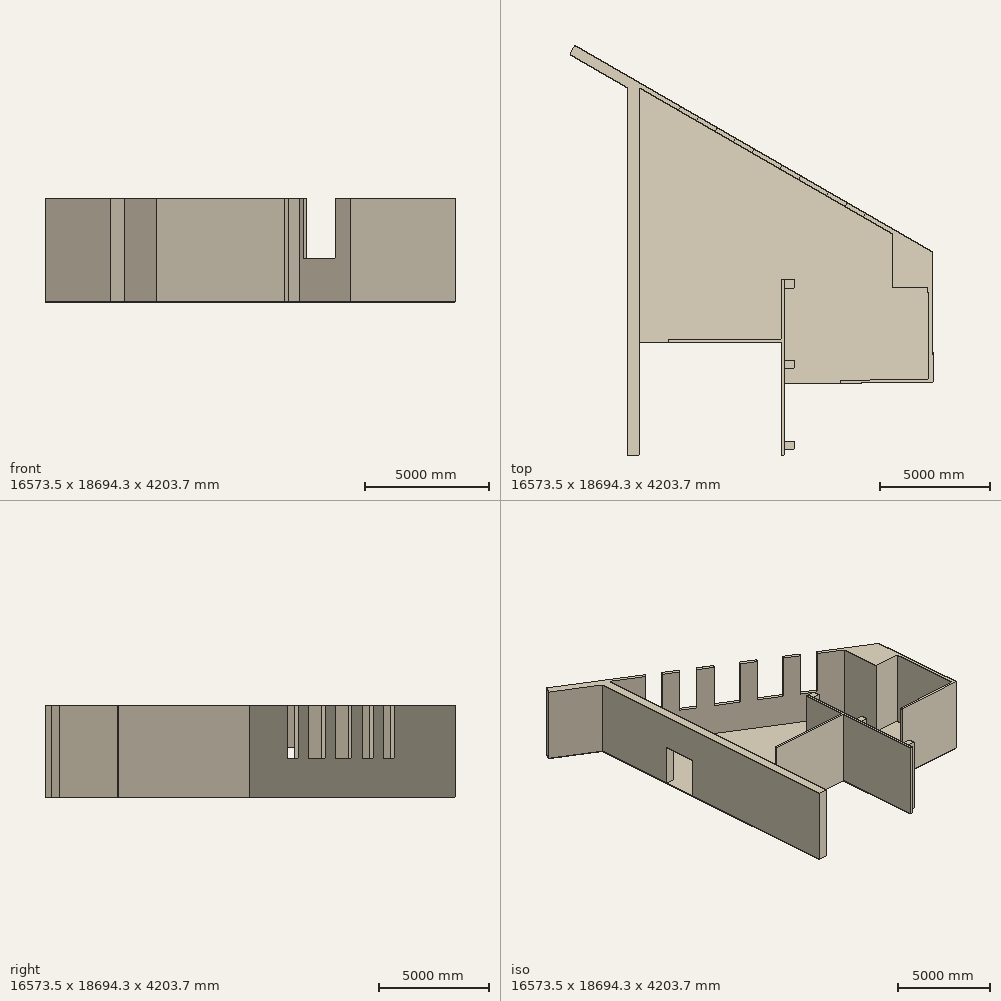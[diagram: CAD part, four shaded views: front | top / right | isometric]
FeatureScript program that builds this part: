
annotation { "Feature Type Name" : "Feature", "Feature Type Description" : "" }
export const myFeature = defineFeature(function(context is Context, id is Id, definition is map)
    precondition{}
    {
        {
            var Q0;
            Q0=qCreatedBy(makeId("Top.planeOp"),FACE);
            var sketch = newSketch(context, id + "F0", { "sketchPlane" : qUnion([Q0])});
            skLineSegment(sketch, "E0.bottom", {"start": v(0, 0) * mm, "end": v(546.1, 0) * mm});
            skLineSegment(sketch, "E0.top", {"start": v(0, 4953) * mm, "end": v(546.1, 4953) * mm});
            skLineSegment(sketch, "E0.left", {"start": v(0, 0) * mm, "end": v(0, 4953) * mm});
            skLineSegment(sketch, "E0.right", {"start": v(546.1, 0) * mm, "end": v(546.1, 4953) * mm});
            skSolve(sketch);
        }
        {
            var Q0;
            Q0 = qSketchRegion(id + "F0", true);
            extrude(context, id + "F1", {"entities" : qUnion([Q0]), "depth" : 4178.3 * mm, "offsetDistance" : 25.4 * mm});
        }
        {
            var Q0;
            Q0=makeQuery(id+"F1.opExtrude","CAP_FACE",FACE,{"disambiguationData":[OSD([sQuery(id+"F0.wireOp",EDGE,"E0.bottom"),sQuery(id+"F0.wireOp",EDGE,"E0.top"),sQuery(id+"F0.wireOp",EDGE,"E0.left"),sQuery(id+"F0.wireOp",EDGE,"E0.right")])],"isStart":false});
            var sketch = newSketch(context, id + "F2", { "sketchPlane" : qUnion([Q0])});
            skLineSegment(sketch, "E1", {"start": v(546.1, 4953) * mm, "end": v(2322.36, 3927.47) * mm});
            skLineSegment(sketch, "E2", {"start": v(2322.36, 3927.47) * mm, "end": v(2423.96, 4103.45) * mm});
            skLineSegment(sketch, "E3", {"start": v(2423.96, 4103.45) * mm, "end": v(-2401.52, 6889.44) * mm});
            skLineSegment(sketch, "E4", {"start": v(-2401.52, 6889.44) * mm, "end": v(-2639.65, 6477) * mm});
            skLineSegment(sketch, "E5", {"start": v(-2639.65, 6477) * mm, "end": v(0, 4953) * mm});
            skSolve(sketch);
        }
        {
            var Q0;
            Q0=makeQuery(id+"F2.imprint","IMPRINT",FACE,{"disambiguationData":[TD([[makeQuery(id+"F2.imprint","IMPRINT",EDGE,{"derivedFrom":sQuery(id+"F2.wireOp",EDGE,"E1")}),1.0]])]});
            var Q1;
            Q1=makeQuery(id+"F1.opExtrude","CAP_FACE",FACE,{"disambiguationData":[OSD([sQuery(id+"F0.wireOp",EDGE,"E0.bottom"),sQuery(id+"F0.wireOp",EDGE,"E0.top"),sQuery(id+"F0.wireOp",EDGE,"E0.left"),sQuery(id+"F0.wireOp",EDGE,"E0.right")])],"isStart":true});
            extrude(context, id + "F3", {"entities" : qUnion([Q0]), "operationType" : NewBodyOperationType.ADD, "endBound" : BoundingType.UP_TO_SURFACE, "oppositeDirection" : true, "depth" : 25.4 * mm, "endBoundEntityFace" : qUnion([Q1]), "offsetDistance" : 25.4 * mm});
        }
        {
            var Q0;
            Q0=makeQuery(id+"F3.opExtrude","SWEPT_FACE",FACE,{"disambiguationData":[OSD([sQuery(id+"F2.wireOp",EDGE,"E2")])]});
            var sketch = newSketch(context, id + "F4", { "sketchPlane" : qUnion([Q0])});
            skLineSegment(sketch, "E6.bottom", {"start": v(4562.47, 0) * mm, "end": v(4765.67, 0) * mm});
            skLineSegment(sketch, "E6.top", {"start": v(4562.47, 1765.3) * mm, "end": v(4765.67, 1765.3) * mm});
            skLineSegment(sketch, "E6.left", {"start": v(4562.47, 0) * mm, "end": v(4562.47, 1765.3) * mm});
            skLineSegment(sketch, "E6.right", {"start": v(4765.67, 0) * mm, "end": v(4765.67, 1765.3) * mm});
            skSolve(sketch);
        }
        {
            var Q0;
            Q0=makeQuery(id+"F4.imprint","IMPRINT",FACE,{"disambiguationData":[TD([[makeQuery(id+"F4.imprint","IMPRINT",EDGE,{"derivedFrom":sQuery(id+"F4.wireOp",EDGE,"E6.bottom")}),-1.0]])]});
            extrude(context, id + "F5", {"entities" : qUnion([Q0]), "operationType" : NewBodyOperationType.ADD, "depth" : 958.85 * mm, "offsetDistance" : 25.4 * mm});
        }
        {
            var Q0;
            Q0=makeQuery(id+"F5.opExtrude","CAP_FACE",FACE,{"disambiguationData":[OSD([sQuery(id+"F4.wireOp",EDGE,"E6.bottom"),sQuery(id+"F4.wireOp",EDGE,"E6.top"),sQuery(id+"F4.wireOp",EDGE,"E6.left"),sQuery(id+"F4.wireOp",EDGE,"E6.right")])],"isStart":false});
            var sketch = newSketch(context, id + "F6", { "sketchPlane" : qUnion([Q0])});
            skLineSegment(sketch, "E7.bottom", {"start": v(4562.47, 0) * mm, "end": v(4765.67, 0) * mm});
            skLineSegment(sketch, "E7.top", {"start": v(4562.47, 4178.3) * mm, "end": v(4765.67, 4178.3) * mm});
            skLineSegment(sketch, "E7.left", {"start": v(4562.47, 0) * mm, "end": v(4562.47, 4178.3) * mm});
            skLineSegment(sketch, "E7.right", {"start": v(4765.67, 0) * mm, "end": v(4765.67, 4178.3) * mm});
            skSolve(sketch);
        }
        {
            var Q0;
            Q0 = qSketchRegion(id + "F6", true);
            extrude(context, id + "F7", {"entities" : qUnion([Q0]), "operationType" : NewBodyOperationType.ADD, "depth" : 965.2 * mm, "offsetDistance" : 25.4 * mm});
        }
        {
            var Q0;
            Q0=makeQuery(id+"F7.opExtrude","CAP_FACE",FACE,{"disambiguationData":[OSD([sQuery(id+"F6.wireOp",EDGE,"E7.bottom"),sQuery(id+"F6.wireOp",EDGE,"E7.top"),sQuery(id+"F6.wireOp",EDGE,"E7.left"),sQuery(id+"F6.wireOp",EDGE,"E7.right")])],"isStart":false});
            var sketch = newSketch(context, id + "F8", { "sketchPlane" : qUnion([Q0])});
            skLineSegment(sketch, "E8.bottom", {"start": v(4562.47, 1765.3) * mm, "end": v(4765.67, 1765.3) * mm});
            skLineSegment(sketch, "E8.top", {"start": v(4562.47, 0) * mm, "end": v(4765.67, 0) * mm});
            skLineSegment(sketch, "E8.left", {"start": v(4562.47, 1765.3) * mm, "end": v(4562.47, 0) * mm});
            skLineSegment(sketch, "E8.right", {"start": v(4765.67, 1765.3) * mm, "end": v(4765.67, 0) * mm});
            skSolve(sketch);
        }
        {
            var Q0;
            Q0=makeQuery(id+"F8.imprint","IMPRINT",FACE,{"disambiguationData":[TD([[makeQuery(id+"F8.imprint","IMPRINT",EDGE,{"derivedFrom":sQuery(id+"F8.wireOp",EDGE,"E8.bottom")}),-1.0]])]});
            extrude(context, id + "F9", {"entities" : qUnion([Q0]), "operationType" : NewBodyOperationType.ADD, "depth" : 965.2 * mm, "offsetDistance" : 25.4 * mm});
        }
        {
            var Q0;
            Q0=makeQuery(id+"F9.opExtrude","CAP_FACE",FACE,{"disambiguationData":[OSD([sQuery(id+"F8.wireOp",EDGE,"E8.bottom"),sQuery(id+"F8.wireOp",EDGE,"E8.top"),sQuery(id+"F8.wireOp",EDGE,"E8.left"),sQuery(id+"F8.wireOp",EDGE,"E8.right")])],"isStart":false});
            var sketch = newSketch(context, id + "F10", { "sketchPlane" : qUnion([Q0])});
            skLineSegment(sketch, "E9.bottom", {"start": v(4562.47, 0) * mm, "end": v(4765.67, 0) * mm});
            skLineSegment(sketch, "E9.top", {"start": v(4562.47, 4178.3) * mm, "end": v(4765.67, 4178.3) * mm});
            skLineSegment(sketch, "E9.left", {"start": v(4562.47, 0) * mm, "end": v(4562.47, 4178.3) * mm});
            skLineSegment(sketch, "E9.right", {"start": v(4765.67, 0) * mm, "end": v(4765.67, 4178.3) * mm});
            skSolve(sketch);
        }
        {
            var Q0;
            Q0 = qSketchRegion(id + "F10", true);
            extrude(context, id + "F11", {"entities" : qUnion([Q0]), "operationType" : NewBodyOperationType.ADD, "depth" : 977.9 * mm, "offsetDistance" : 25.4 * mm});
        }
        {
            var Q0;
            Q0=makeQuery(id+"F11.opExtrude","CAP_FACE",FACE,{"disambiguationData":[OSD([sQuery(id+"F10.wireOp",EDGE,"E9.bottom"),sQuery(id+"F10.wireOp",EDGE,"E9.top"),sQuery(id+"F10.wireOp",EDGE,"E9.left"),sQuery(id+"F10.wireOp",EDGE,"E9.right")])],"isStart":false});
            var sketch = newSketch(context, id + "F12", { "sketchPlane" : qUnion([Q0])});
            skLineSegment(sketch, "E10.bottom", {"start": v(4562.47, 0) * mm, "end": v(4765.67, 0) * mm});
            skLineSegment(sketch, "E10.top", {"start": v(4562.47, 1765.3) * mm, "end": v(4765.67, 1765.3) * mm});
            skLineSegment(sketch, "E10.left", {"start": v(4562.47, 0) * mm, "end": v(4562.47, 1765.3) * mm});
            skLineSegment(sketch, "E10.right", {"start": v(4765.67, 0) * mm, "end": v(4765.67, 1765.3) * mm});
            skSolve(sketch);
        }
        {
            var Q0;
            Q0 = qSketchRegion(id + "F12", true);
            extrude(context, id + "F13", {"entities" : qUnion([Q0]), "operationType" : NewBodyOperationType.ADD, "depth" : 1473.2 * mm, "offsetDistance" : 25.4 * mm});
        }
        {
            var Q0;
            Q0=makeQuery(id+"F13.opExtrude","CAP_FACE",FACE,{"disambiguationData":[OSD([sQuery(id+"F12.wireOp",EDGE,"E10.bottom"),sQuery(id+"F12.wireOp",EDGE,"E10.top"),sQuery(id+"F12.wireOp",EDGE,"E10.left"),sQuery(id+"F12.wireOp",EDGE,"E10.right")])],"isStart":false});
            var sketch = newSketch(context, id + "F14", { "sketchPlane" : qUnion([Q0])});
            skLineSegment(sketch, "E11.bottom", {"start": v(4562.47, 0) * mm, "end": v(4765.67, 0) * mm});
            skLineSegment(sketch, "E11.top", {"start": v(4562.47, 4178.3) * mm, "end": v(4765.67, 4178.3) * mm});
            skLineSegment(sketch, "E11.left", {"start": v(4562.47, 0) * mm, "end": v(4562.47, 4178.3) * mm});
            skLineSegment(sketch, "E11.right", {"start": v(4765.67, 0) * mm, "end": v(4765.67, 4178.3) * mm});
            skSolve(sketch);
        }
        {
            var Q0;
            Q0 = qSketchRegion(id + "F14", true);
            extrude(context, id + "F15", {"entities" : qUnion([Q0]), "operationType" : NewBodyOperationType.ADD, "depth" : 977.9 * mm, "offsetDistance" : 25.4 * mm});
        }
        {
            var Q0;
            Q0=makeQuery(id+"F15.opExtrude","CAP_FACE",FACE,{"disambiguationData":[OSD([sQuery(id+"F14.wireOp",EDGE,"E11.bottom"),sQuery(id+"F14.wireOp",EDGE,"E11.top"),sQuery(id+"F14.wireOp",EDGE,"E11.left"),sQuery(id+"F14.wireOp",EDGE,"E11.right")])],"isStart":false});
            var sketch = newSketch(context, id + "F16", { "sketchPlane" : qUnion([Q0])});
            skLineSegment(sketch, "E12.bottom", {"start": v(4562.47, 0) * mm, "end": v(4765.67, 0) * mm});
            skLineSegment(sketch, "E12.top", {"start": v(4562.47, 1765.3) * mm, "end": v(4765.67, 1765.3) * mm});
            skLineSegment(sketch, "E12.left", {"start": v(4562.47, 0) * mm, "end": v(4562.47, 1765.3) * mm});
            skLineSegment(sketch, "E12.right", {"start": v(4765.67, 0) * mm, "end": v(4765.67, 1765.3) * mm});
            skSolve(sketch);
        }
        {
            var Q0;
            Q0 = qSketchRegion(id + "F16", true);
            extrude(context, id + "F17", {"entities" : qUnion([Q0]), "operationType" : NewBodyOperationType.ADD, "depth" : 1473.2 * mm, "offsetDistance" : 25.4 * mm});
        }
        {
            var Q0;
            Q0=makeQuery(id+"F17.opExtrude","CAP_FACE",FACE,{"disambiguationData":[OSD([sQuery(id+"F16.wireOp",EDGE,"E12.bottom"),sQuery(id+"F16.wireOp",EDGE,"E12.top"),sQuery(id+"F16.wireOp",EDGE,"E12.left"),sQuery(id+"F16.wireOp",EDGE,"E12.right")])],"isStart":false});
            var sketch = newSketch(context, id + "F18", { "sketchPlane" : qUnion([Q0])});
            skLineSegment(sketch, "E13.bottom", {"start": v(4562.47, 0) * mm, "end": v(4765.67, 0) * mm});
            skLineSegment(sketch, "E13.top", {"start": v(4562.47, 4178.3) * mm, "end": v(4765.67, 4178.3) * mm});
            skLineSegment(sketch, "E13.left", {"start": v(4562.47, 0) * mm, "end": v(4562.47, 4178.3) * mm});
            skLineSegment(sketch, "E13.right", {"start": v(4765.67, 0) * mm, "end": v(4765.67, 4178.3) * mm});
            skSolve(sketch);
        }
        {
            var Q0;
            Q0 = qSketchRegion(id + "F18", true);
            extrude(context, id + "F19", {"entities" : qUnion([Q0]), "operationType" : NewBodyOperationType.ADD, "depth" : 977.9 * mm, "offsetDistance" : 25.4 * mm});
        }
        {
            var Q0;
            Q0=makeQuery(id+"F19.opExtrude","CAP_FACE",FACE,{"disambiguationData":[OSD([sQuery(id+"F18.wireOp",EDGE,"E13.bottom"),sQuery(id+"F18.wireOp",EDGE,"E13.top"),sQuery(id+"F18.wireOp",EDGE,"E13.left"),sQuery(id+"F18.wireOp",EDGE,"E13.right")])],"isStart":false});
            var sketch = newSketch(context, id + "F20", { "sketchPlane" : qUnion([Q0])});
            skLineSegment(sketch, "E14.bottom", {"start": v(4562.47, 0) * mm, "end": v(4765.67, 0) * mm});
            skLineSegment(sketch, "E14.top", {"start": v(4562.47, 1765.3) * mm, "end": v(4765.67, 1765.3) * mm});
            skLineSegment(sketch, "E14.left", {"start": v(4562.47, 0) * mm, "end": v(4562.47, 1765.3) * mm});
            skLineSegment(sketch, "E14.right", {"start": v(4765.67, 0) * mm, "end": v(4765.67, 1765.3) * mm});
            skSolve(sketch);
        }
        {
            var Q0;
            Q0 = qSketchRegion(id + "F20", true);
            extrude(context, id + "F21", {"entities" : qUnion([Q0]), "operationType" : NewBodyOperationType.ADD, "depth" : 958.85 * mm, "offsetDistance" : 25.4 * mm});
        }
        {
            var Q0;
            Q0=makeQuery(id+"F21.opExtrude","CAP_FACE",FACE,{"disambiguationData":[OSD([sQuery(id+"F20.wireOp",EDGE,"E14.bottom"),sQuery(id+"F20.wireOp",EDGE,"E14.top"),sQuery(id+"F20.wireOp",EDGE,"E14.left"),sQuery(id+"F20.wireOp",EDGE,"E14.right")])],"isStart":false});
            var sketch = newSketch(context, id + "F22", { "sketchPlane" : qUnion([Q0])});
            skLineSegment(sketch, "E15.bottom", {"start": v(4562.47, 0) * mm, "end": v(4765.67, 0) * mm});
            skLineSegment(sketch, "E15.top", {"start": v(4562.47, 4178.3) * mm, "end": v(4765.67, 4178.3) * mm});
            skLineSegment(sketch, "E15.left", {"start": v(4562.47, 0) * mm, "end": v(4562.47, 4178.3) * mm});
            skLineSegment(sketch, "E15.right", {"start": v(4765.67, 0) * mm, "end": v(4765.67, 4178.3) * mm});
            skSolve(sketch);
        }
        {
            var Q0;
            {var subQ0=sQuery(id+"F22.wireOp",EDGE,"E15.bottom");Q0=makeQuery(id+"F22.imprint","IMPRINT",FACE,{"disambiguationData":[TD([[makeQuery(id+"F22.imprint","IMPRINT",EDGE,{"derivedFrom":subQ0}),-1.0]])]});}
            var Q1;
            {var subQ0=sQuery(id+"F22.wireOp",EDGE,"E15.top");Q1=makeQuery(id+"F22.imprint","IMPRINT",FACE,{"disambiguationData":[TD([[makeQuery(id+"F22.imprint","IMPRINT",EDGE,{"derivedFrom":subQ0}),-1.0]])]});}
            extrude(context, id + "F23", {"entities" : qUnion([Q0, Q1]), "operationType" : NewBodyOperationType.ADD, "depth" : 1524 * mm, "offsetDistance" : 25.4 * mm});
        }
        {
            var Q0;
            Q0=makeQuery(id+"F23.opExtrude","SWEPT_FACE",FACE,{"disambiguationData":[OSD([sQuery(id+"F22.wireOp",EDGE,"E15.top")])]});
            var sketch = newSketch(context, id + "F24", { "sketchPlane" : qUnion([Q0])});
            skLineSegment(sketch, "E16", {"start": v(12067.05, -1698.63) * mm, "end": v(12067.05, -4137.03) * mm});
            skLineSegment(sketch, "E17", {"start": v(12067.05, -4137.03) * mm, "end": v(13692.6, -4122.79) * mm});
            skLineSegment(sketch, "E18", {"start": v(13692.6, -4122.79) * mm, "end": v(13729.52, -8339.02) * mm});
            skLineSegment(sketch, "E19", {"start": v(13729.52, -8339.02) * mm, "end": v(13932.71, -8337.24) * mm});
            skLineSegment(sketch, "E20", {"start": v(13932.71, -8337.24) * mm, "end": v(13881.69, -2511.67) * mm});
            skLineSegment(sketch, "E21", {"start": v(13881.69, -2511.67) * mm, "end": v(12168.65, -1522.65) * mm});
            skSolve(sketch);
        }
        {
            var Q0;
            Q0=makeQuery(id+"F24.imprint","IMPRINT",FACE,{"disambiguationData":[TD([[makeQuery(id+"F24.imprint","IMPRINT",EDGE,{"derivedFrom":sQuery(id+"F24.wireOp",EDGE,"E16")}),1.0]])]});
            var Q1;
            {var subQ0=sQuery(id+"F0.wireOp",EDGE,"E0.right");var subQ1=sQuery(id+"F0.wireOp",EDGE,"E0.left");var subQ2=sQuery(id+"F0.wireOp",EDGE,"E0.top");var subQ3=sQuery(id+"F0.wireOp",EDGE,"E0.bottom");Q1=makeQuery(id+"F23.boolean.opBoolean","MERGE",FACE,{"derivedFrom":[makeQuery(id+"F21.boolean.opBoolean","MERGE",FACE,{"derivedFrom":[makeQuery(id+"F19.boolean.opBoolean","MERGE",FACE,{"derivedFrom":[makeQuery(id+"F17.boolean.opBoolean","MERGE",FACE,{"derivedFrom":[makeQuery(id+"F15.boolean.opBoolean","MERGE",FACE,{"derivedFrom":[makeQuery(id+"F13.boolean.opBoolean","MERGE",FACE,{"derivedFrom":[makeQuery(id+"F11.boolean.opBoolean","MERGE",FACE,{"derivedFrom":[makeQuery(id+"F9.boolean.opBoolean","MERGE",FACE,{"derivedFrom":[makeQuery(id+"F7.boolean.opBoolean","MERGE",FACE,{"derivedFrom":[makeQuery(id+"F5.boolean.opBoolean","MERGE",FACE,{"derivedFrom":[makeQuery(id+"F3.boolean.opBoolean","MERGE",FACE,{"derivedFrom":[makeQuery(id+"F1.opExtrude","CAP_FACE",FACE,{"disambiguationData":[OSD([subQ3,subQ2,subQ1,subQ0])],"isStart":true}),makeQuery(id+"F3.opExtrude","CAP_FACE",FACE,{"disambiguationData":[OSD([subQ3,subQ2,subQ1,subQ0])],"isStart":false})]}),makeQuery(id+"F5.opExtrude","SWEPT_FACE",FACE,{"disambiguationData":[OSD([sQuery(id+"F4.wireOp",EDGE,"E6.bottom")])]})]}),makeQuery(id+"F7.opExtrude","SWEPT_FACE",FACE,{"disambiguationData":[OSD([sQuery(id+"F6.wireOp",EDGE,"E7.bottom")])]})]}),makeQuery(id+"F9.opExtrude","SWEPT_FACE",FACE,{"disambiguationData":[OSD([sQuery(id+"F8.wireOp",EDGE,"E8.top")])]})]}),makeQuery(id+"F11.opExtrude","SWEPT_FACE",FACE,{"disambiguationData":[OSD([sQuery(id+"F10.wireOp",EDGE,"E9.bottom")])]})]}),makeQuery(id+"F13.opExtrude","SWEPT_FACE",FACE,{"disambiguationData":[OSD([sQuery(id+"F12.wireOp",EDGE,"E10.bottom")])]})]}),makeQuery(id+"F15.opExtrude","SWEPT_FACE",FACE,{"disambiguationData":[OSD([sQuery(id+"F14.wireOp",EDGE,"E11.bottom")])]})]}),makeQuery(id+"F17.opExtrude","SWEPT_FACE",FACE,{"disambiguationData":[OSD([sQuery(id+"F16.wireOp",EDGE,"E12.bottom")])]})]}),makeQuery(id+"F19.opExtrude","SWEPT_FACE",FACE,{"disambiguationData":[OSD([sQuery(id+"F18.wireOp",EDGE,"E13.bottom")])]})]}),makeQuery(id+"F21.opExtrude","SWEPT_FACE",FACE,{"disambiguationData":[OSD([sQuery(id+"F20.wireOp",EDGE,"E14.bottom")])]})]}),makeQuery(id+"F23.opExtrude","SWEPT_FACE",FACE,{"disambiguationData":[OSD([sQuery(id+"F22.wireOp",EDGE,"E15.bottom")])]})]});}
            extrude(context, id + "F25", {"entities" : qUnion([Q0]), "operationType" : NewBodyOperationType.ADD, "endBound" : BoundingType.UP_TO_SURFACE, "oppositeDirection" : true, "depth" : 25.4 * mm, "endBoundEntityFace" : qUnion([Q1]), "offsetDistance" : 25.4 * mm});
        }
        {
            var Q0;
            {var subQ0=sQuery(id+"F22.wireOp",EDGE,"E15.top");Q0=makeQuery(id+"F25.boolean.opBoolean","MERGE",FACE,{"derivedFrom":[makeQuery(id+"F23.opExtrude","SWEPT_FACE",FACE,{"disambiguationData":[OSD([subQ0])]}),makeQuery(id+"F25.opExtrude","CAP_FACE",FACE,{"disambiguationData":[OSD([subQ0,sQuery(id+"F24.wireOp",EDGE,"E16"),sQuery(id+"F24.wireOp",EDGE,"E17"),sQuery(id+"F24.wireOp",EDGE,"E18"),sQuery(id+"F24.wireOp",EDGE,"E19"),sQuery(id+"F24.wireOp",EDGE,"E20"),sQuery(id+"F24.wireOp",EDGE,"E21")])],"isStart":true})]});}
            var sketch = newSketch(context, id + "F26", { "sketchPlane" : qUnion([Q0])});
            skLineSegment(sketch, "E22.bottom", {"start": v(7164.85, -3795.07) * mm, "end": v(7609.35, -3795.07) * mm});
            skLineSegment(sketch, "E22.top", {"start": v(7164.85, -4176.07) * mm, "end": v(7609.35, -4176.07) * mm});
            skLineSegment(sketch, "E22.left", {"start": v(7164.85, -3795.07) * mm, "end": v(7164.85, -4176.07) * mm});
            skLineSegment(sketch, "E22.right", {"start": v(7609.35, -3795.07) * mm, "end": v(7609.35, -4176.07) * mm});
            skLineSegment(sketch, "E23.bottom", {"start": v(7164.85, -7478.07) * mm, "end": v(7609.35, -7478.07) * mm});
            skLineSegment(sketch, "E23.top", {"start": v(7164.85, -7859.07) * mm, "end": v(7609.35, -7859.07) * mm});
            skLineSegment(sketch, "E23.left", {"start": v(7164.85, -7478.07) * mm, "end": v(7164.85, -7859.07) * mm});
            skLineSegment(sketch, "E23.right", {"start": v(7609.35, -7478.07) * mm, "end": v(7609.35, -7859.07) * mm});
            skLineSegment(sketch, "E24.bottom", {"start": v(7164.85, -11148.37) * mm, "end": v(7609.35, -11148.37) * mm});
            skLineSegment(sketch, "E24.top", {"start": v(7164.85, -11529.37) * mm, "end": v(7609.35, -11529.37) * mm});
            skLineSegment(sketch, "E24.left", {"start": v(7164.85, -11148.37) * mm, "end": v(7164.85, -11529.37) * mm});
            skLineSegment(sketch, "E24.right", {"start": v(7609.35, -11148.37) * mm, "end": v(7609.35, -11529.37) * mm});
            skSolve(sketch);
        }
        {
            var Q0;
            Q0 = qSketchRegion(id + "F26", true);
            var Q1;
            {var subQ0=sQuery(id+"F22.wireOp",EDGE,"E15.bottom");var subQ1=sQuery(id+"F20.wireOp",EDGE,"E14.bottom");var subQ2=sQuery(id+"F18.wireOp",EDGE,"E13.bottom");var subQ3=sQuery(id+"F16.wireOp",EDGE,"E12.bottom");var subQ4=sQuery(id+"F14.wireOp",EDGE,"E11.bottom");var subQ5=sQuery(id+"F12.wireOp",EDGE,"E10.bottom");var subQ6=sQuery(id+"F10.wireOp",EDGE,"E9.bottom");var subQ7=sQuery(id+"F8.wireOp",EDGE,"E8.top");var subQ8=sQuery(id+"F6.wireOp",EDGE,"E7.bottom");var subQ9=sQuery(id+"F4.wireOp",EDGE,"E6.bottom");var subQ10=sQuery(id+"F0.wireOp",EDGE,"E0.right");var subQ11=sQuery(id+"F0.wireOp",EDGE,"E0.left");var subQ12=sQuery(id+"F0.wireOp",EDGE,"E0.top");var subQ13=sQuery(id+"F0.wireOp",EDGE,"E0.bottom");Q1=makeQuery(id+"F25.boolean.opBoolean","MERGE",FACE,{"derivedFrom":[makeQuery(id+"F23.boolean.opBoolean","MERGE",FACE,{"derivedFrom":[makeQuery(id+"F21.boolean.opBoolean","MERGE",FACE,{"derivedFrom":[makeQuery(id+"F19.boolean.opBoolean","MERGE",FACE,{"derivedFrom":[makeQuery(id+"F17.boolean.opBoolean","MERGE",FACE,{"derivedFrom":[makeQuery(id+"F15.boolean.opBoolean","MERGE",FACE,{"derivedFrom":[makeQuery(id+"F13.boolean.opBoolean","MERGE",FACE,{"derivedFrom":[makeQuery(id+"F11.boolean.opBoolean","MERGE",FACE,{"derivedFrom":[makeQuery(id+"F9.boolean.opBoolean","MERGE",FACE,{"derivedFrom":[makeQuery(id+"F7.boolean.opBoolean","MERGE",FACE,{"derivedFrom":[makeQuery(id+"F5.boolean.opBoolean","MERGE",FACE,{"derivedFrom":[makeQuery(id+"F3.boolean.opBoolean","MERGE",FACE,{"derivedFrom":[makeQuery(id+"F1.opExtrude","CAP_FACE",FACE,{"disambiguationData":[OSD([subQ13,subQ12,subQ11,subQ10])],"isStart":true}),makeQuery(id+"F3.opExtrude","CAP_FACE",FACE,{"disambiguationData":[OSD([subQ13,subQ12,subQ11,subQ10])],"isStart":false})]}),makeQuery(id+"F5.opExtrude","SWEPT_FACE",FACE,{"disambiguationData":[OSD([subQ9])]})]}),makeQuery(id+"F7.opExtrude","SWEPT_FACE",FACE,{"disambiguationData":[OSD([subQ8])]})]}),makeQuery(id+"F9.opExtrude","SWEPT_FACE",FACE,{"disambiguationData":[OSD([subQ7])]})]}),makeQuery(id+"F11.opExtrude","SWEPT_FACE",FACE,{"disambiguationData":[OSD([subQ6])]})]}),makeQuery(id+"F13.opExtrude","SWEPT_FACE",FACE,{"disambiguationData":[OSD([subQ5])]})]}),makeQuery(id+"F15.opExtrude","SWEPT_FACE",FACE,{"disambiguationData":[OSD([subQ4])]})]}),makeQuery(id+"F17.opExtrude","SWEPT_FACE",FACE,{"disambiguationData":[OSD([subQ3])]})]}),makeQuery(id+"F19.opExtrude","SWEPT_FACE",FACE,{"disambiguationData":[OSD([subQ2])]})]}),makeQuery(id+"F21.opExtrude","SWEPT_FACE",FACE,{"disambiguationData":[OSD([subQ1])]})]}),makeQuery(id+"F23.opExtrude","SWEPT_FACE",FACE,{"disambiguationData":[OSD([subQ0])]})]}),makeQuery(id+"F25.opExtrude","CAP_FACE",FACE,{"disambiguationData":[OSD([subQ13,subQ12,subQ11,subQ10,subQ9,subQ8,subQ7,subQ6,subQ5,subQ4,subQ3,subQ2,subQ1,subQ0])],"isStart":false})]});}
            extrude(context, id + "F27", {"entities" : qUnion([Q0]), "endBound" : BoundingType.UP_TO_SURFACE, "oppositeDirection" : true, "depth" : 25.4 * mm, "endBoundEntityFace" : qUnion([Q1]), "offsetDistance" : 25.4 * mm});
        }
        {
            var Q0;
            Q0=makeQuery(id+"F25.opExtrude","SWEPT_FACE",FACE,{"disambiguationData":[OSD([sQuery(id+"F24.wireOp",EDGE,"E20")])]});
            var sketch = newSketch(context, id + "F28", { "sketchPlane" : qUnion([Q0])});
            skLineSegment(sketch, "E25.bottom", {"start": v(-8458.96, 0) * mm, "end": v(-8592.31, 0) * mm});
            skLineSegment(sketch, "E25.top", {"start": v(-8458.96, 4178.3) * mm, "end": v(-8592.31, 4178.3) * mm});
            skLineSegment(sketch, "E25.left", {"start": v(-8458.96, 0) * mm, "end": v(-8458.96, 4178.3) * mm});
            skLineSegment(sketch, "E25.right", {"start": v(-8592.31, 0) * mm, "end": v(-8592.31, 4178.3) * mm});
            skSolve(sketch);
        }
        {
            var Q0;
            Q0 = qSketchRegion(id + "F28", true);
            extrude(context, id + "F29", {"entities" : qUnion([Q0]), "operationType" : NewBodyOperationType.ADD, "oppositeDirection" : true, "depth" : 4241.8 * mm, "offsetDistance" : 25.4 * mm});
        }
        {
            var Q0;
            Q0=makeQuery(id+"F27.opExtrude","CAP_FACE",FACE,{"disambiguationData":[OSD([sQuery(id+"F26.wireOp",EDGE,"E22.bottom"),sQuery(id+"F26.wireOp",EDGE,"E22.top"),sQuery(id+"F26.wireOp",EDGE,"E22.left"),sQuery(id+"F26.wireOp",EDGE,"E22.right")])],"isStart":true});
            var sketch = newSketch(context, id + "F30", { "sketchPlane" : qUnion([Q0])});
            skLineSegment(sketch, "E26.bottom", {"start": v(7164.85, -3795.07) * mm, "end": v(7031.5, -3795.07) * mm});
            skLineSegment(sketch, "E26.top", {"start": v(7164.85, -11804.9) * mm, "end": v(7031.5, -11804.9) * mm});
            skLineSegment(sketch, "E26.left", {"start": v(7164.85, -3795.07) * mm, "end": v(7164.85, -11804.9) * mm});
            skLineSegment(sketch, "E26.right", {"start": v(7031.5, -3795.07) * mm, "end": v(7031.5, -11804.9) * mm});
            skSolve(sketch);
        }
        {
            var Q0;
            Q0 = qSketchRegion(id + "F30", true);
            var Q1;
            {var subQ0=sQuery(id+"F22.wireOp",EDGE,"E15.bottom");var subQ1=sQuery(id+"F20.wireOp",EDGE,"E14.bottom");var subQ2=sQuery(id+"F18.wireOp",EDGE,"E13.bottom");var subQ3=sQuery(id+"F16.wireOp",EDGE,"E12.bottom");var subQ4=sQuery(id+"F14.wireOp",EDGE,"E11.bottom");var subQ5=sQuery(id+"F12.wireOp",EDGE,"E10.bottom");var subQ6=sQuery(id+"F10.wireOp",EDGE,"E9.bottom");var subQ7=sQuery(id+"F8.wireOp",EDGE,"E8.top");var subQ8=sQuery(id+"F6.wireOp",EDGE,"E7.bottom");var subQ9=sQuery(id+"F4.wireOp",EDGE,"E6.bottom");var subQ10=sQuery(id+"F0.wireOp",EDGE,"E0.right");var subQ11=sQuery(id+"F0.wireOp",EDGE,"E0.left");var subQ12=sQuery(id+"F0.wireOp",EDGE,"E0.top");var subQ13=sQuery(id+"F0.wireOp",EDGE,"E0.bottom");Q1=makeQuery(id+"F29.boolean.opBoolean","MERGE",FACE,{"derivedFrom":[makeQuery(id+"F25.boolean.opBoolean","MERGE",FACE,{"derivedFrom":[makeQuery(id+"F23.boolean.opBoolean","MERGE",FACE,{"derivedFrom":[makeQuery(id+"F21.boolean.opBoolean","MERGE",FACE,{"derivedFrom":[makeQuery(id+"F19.boolean.opBoolean","MERGE",FACE,{"derivedFrom":[makeQuery(id+"F17.boolean.opBoolean","MERGE",FACE,{"derivedFrom":[makeQuery(id+"F15.boolean.opBoolean","MERGE",FACE,{"derivedFrom":[makeQuery(id+"F13.boolean.opBoolean","MERGE",FACE,{"derivedFrom":[makeQuery(id+"F11.boolean.opBoolean","MERGE",FACE,{"derivedFrom":[makeQuery(id+"F9.boolean.opBoolean","MERGE",FACE,{"derivedFrom":[makeQuery(id+"F7.boolean.opBoolean","MERGE",FACE,{"derivedFrom":[makeQuery(id+"F5.boolean.opBoolean","MERGE",FACE,{"derivedFrom":[makeQuery(id+"F3.boolean.opBoolean","MERGE",FACE,{"derivedFrom":[makeQuery(id+"F1.opExtrude","CAP_FACE",FACE,{"disambiguationData":[OSD([subQ13,subQ12,subQ11,subQ10])],"isStart":true}),makeQuery(id+"F3.opExtrude","CAP_FACE",FACE,{"disambiguationData":[OSD([subQ13,subQ12,subQ11,subQ10])],"isStart":false})]}),makeQuery(id+"F5.opExtrude","SWEPT_FACE",FACE,{"disambiguationData":[OSD([subQ9])]})]}),makeQuery(id+"F7.opExtrude","SWEPT_FACE",FACE,{"disambiguationData":[OSD([subQ8])]})]}),makeQuery(id+"F9.opExtrude","SWEPT_FACE",FACE,{"disambiguationData":[OSD([subQ7])]})]}),makeQuery(id+"F11.opExtrude","SWEPT_FACE",FACE,{"disambiguationData":[OSD([subQ6])]})]}),makeQuery(id+"F13.opExtrude","SWEPT_FACE",FACE,{"disambiguationData":[OSD([subQ5])]})]}),makeQuery(id+"F15.opExtrude","SWEPT_FACE",FACE,{"disambiguationData":[OSD([subQ4])]})]}),makeQuery(id+"F17.opExtrude","SWEPT_FACE",FACE,{"disambiguationData":[OSD([subQ3])]})]}),makeQuery(id+"F19.opExtrude","SWEPT_FACE",FACE,{"disambiguationData":[OSD([subQ2])]})]}),makeQuery(id+"F21.opExtrude","SWEPT_FACE",FACE,{"disambiguationData":[OSD([subQ1])]})]}),makeQuery(id+"F23.opExtrude","SWEPT_FACE",FACE,{"disambiguationData":[OSD([subQ0])]})]}),makeQuery(id+"F25.opExtrude","CAP_FACE",FACE,{"disambiguationData":[OSD([subQ13,subQ12,subQ11,subQ10,subQ9,subQ8,subQ7,subQ6,subQ5,subQ4,subQ3,subQ2,subQ1,subQ0])],"isStart":false})]}),makeQuery(id+"F29.opExtrude","SWEPT_FACE",FACE,{"disambiguationData":[OSD([sQuery(id+"F28.wireOp",EDGE,"E25.bottom")])]})]});}
            extrude(context, id + "F31", {"entities" : qUnion([Q0]), "endBound" : BoundingType.UP_TO_SURFACE, "oppositeDirection" : true, "depth" : 25.4 * mm, "endBoundEntityFace" : qUnion([Q1]), "offsetDistance" : 25.4 * mm});
        }
        {
            var Q0;
            Q0=makeQuery(id+"F31.opExtrude","SWEPT_FACE",FACE,{"disambiguationData":[OSD([sQuery(id+"F30.wireOp",EDGE,"E26.right")])]});
            var sketch = newSketch(context, id + "F32", { "sketchPlane" : qUnion([Q0])});
            skLineSegment(sketch, "E27.bottom", {"start": v(6512.87, 4178.3) * mm, "end": v(6646.22, 4178.3) * mm});
            skLineSegment(sketch, "E27.top", {"start": v(6512.87, 0) * mm, "end": v(6646.22, 0) * mm});
            skLineSegment(sketch, "E27.left", {"start": v(6512.87, 4178.3) * mm, "end": v(6512.87, 0) * mm});
            skLineSegment(sketch, "E27.right", {"start": v(6646.22, 4178.3) * mm, "end": v(6646.22, 0) * mm});
            skSolve(sketch);
        }
        {
            var Q0;
            Q0 = qSketchRegion(id + "F32", true);
            extrude(context, id + "F33", {"entities" : qUnion([Q0]), "operationType" : NewBodyOperationType.ADD, "depth" : 5168.9 * mm, "offsetDistance" : 25.4 * mm});
        }
        {
            var Q0;
            Q0=makeQuery(id+"F1.opExtrude","SWEPT_FACE",FACE,{"disambiguationData":[OSD([sQuery(id+"F0.wireOp",EDGE,"E0.bottom")])]});
            var sketch = newSketch(context, id + "F34", { "sketchPlane" : qUnion([Q0])});
            skLineSegment(sketch, "E28.bottom", {"start": v(0, 4178.3) * mm, "end": v(546.1, 4178.3) * mm});
            skLineSegment(sketch, "E28.top", {"start": v(0, 2260.6) * mm, "end": v(546.1, 2260.6) * mm});
            skLineSegment(sketch, "E28.left", {"start": v(0, 4178.3) * mm, "end": v(0, 2260.6) * mm});
            skLineSegment(sketch, "E28.right", {"start": v(546.1, 4178.3) * mm, "end": v(546.1, 2260.6) * mm});
            skSolve(sketch);
        }
        {
            var Q0;
            Q0=makeQuery(id+"F34.imprint","IMPRINT",FACE,{"disambiguationData":[TD([[makeQuery(id+"F34.imprint","IMPRINT",EDGE,{"derivedFrom":sQuery(id+"F34.wireOp",EDGE,"E28.bottom")}),-1.0]])]});
            extrude(context, id + "F35", {"entities" : qUnion([Q0]), "operationType" : NewBodyOperationType.ADD, "depth" : 1981.2 * mm, "offsetDistance" : 25.4 * mm});
        }
        {
            var Q0;
            Q0=makeQuery(id+"F35.opExtrude","CAP_FACE",FACE,{"disambiguationData":[OSD([sQuery(id+"F34.wireOp",EDGE,"E28.bottom"),sQuery(id+"F34.wireOp",EDGE,"E28.top"),sQuery(id+"F34.wireOp",EDGE,"E28.left"),sQuery(id+"F34.wireOp",EDGE,"E28.right")])],"isStart":false});
            var sketch = newSketch(context, id + "F36", { "sketchPlane" : qUnion([Q0])});
            skLineSegment(sketch, "E29.bottom", {"start": v(0, 4178.3) * mm, "end": v(546.1, 4178.3) * mm});
            skLineSegment(sketch, "E29.top", {"start": v(0, 0) * mm, "end": v(546.1, 0) * mm});
            skLineSegment(sketch, "E29.left", {"start": v(0, 4178.3) * mm, "end": v(0, 0) * mm});
            skLineSegment(sketch, "E29.right", {"start": v(546.1, 4178.3) * mm, "end": v(546.1, 0) * mm});
            skSolve(sketch);
        }
        {
            var Q0;
            {var subQ0=sQuery(id+"F36.wireOp",EDGE,"E29.top");Q0=makeQuery(id+"F36.imprint","IMPRINT",FACE,{"disambiguationData":[TD([[makeQuery(id+"F36.imprint","IMPRINT",EDGE,{"derivedFrom":subQ0}),1.0]])]});}
            var Q1;
            {var subQ0=sQuery(id+"F36.wireOp",EDGE,"E29.bottom");Q1=makeQuery(id+"F36.imprint","IMPRINT",FACE,{"disambiguationData":[TD([[makeQuery(id+"F36.imprint","IMPRINT",EDGE,{"derivedFrom":subQ0}),-1.0]])]});}
            var Q2;
            Q2=makeQuery(id+"F31.opExtrude","SWEPT_FACE",FACE,{"disambiguationData":[OSD([sQuery(id+"F30.wireOp",EDGE,"E26.top")])]});
            extrude(context, id + "F37", {"entities" : qUnion([Q0, Q1]), "operationType" : NewBodyOperationType.ADD, "endBound" : BoundingType.UP_TO_SURFACE, "depth" : 25.4 * mm, "endBoundEntityFace" : qUnion([Q2]), "offsetDistance" : 25.4 * mm});
        }
        {
            var Q0;
            {var subQ0=sQuery(id+"F22.wireOp",EDGE,"E15.bottom");var subQ1=sQuery(id+"F20.wireOp",EDGE,"E14.bottom");var subQ2=sQuery(id+"F18.wireOp",EDGE,"E13.bottom");var subQ3=sQuery(id+"F16.wireOp",EDGE,"E12.bottom");var subQ4=sQuery(id+"F14.wireOp",EDGE,"E11.bottom");var subQ5=sQuery(id+"F12.wireOp",EDGE,"E10.bottom");var subQ6=sQuery(id+"F10.wireOp",EDGE,"E9.bottom");var subQ7=sQuery(id+"F8.wireOp",EDGE,"E8.top");var subQ8=sQuery(id+"F6.wireOp",EDGE,"E7.bottom");var subQ9=sQuery(id+"F4.wireOp",EDGE,"E6.bottom");var subQ10=sQuery(id+"F0.wireOp",EDGE,"E0.right");var subQ11=sQuery(id+"F0.wireOp",EDGE,"E0.left");var subQ12=sQuery(id+"F0.wireOp",EDGE,"E0.top");var subQ13=sQuery(id+"F0.wireOp",EDGE,"E0.bottom");Q0=makeQuery(id+"F29.boolean.opBoolean","MERGE",FACE,{"derivedFrom":[makeQuery(id+"F25.boolean.opBoolean","MERGE",FACE,{"derivedFrom":[makeQuery(id+"F23.boolean.opBoolean","MERGE",FACE,{"derivedFrom":[makeQuery(id+"F21.boolean.opBoolean","MERGE",FACE,{"derivedFrom":[makeQuery(id+"F19.boolean.opBoolean","MERGE",FACE,{"derivedFrom":[makeQuery(id+"F17.boolean.opBoolean","MERGE",FACE,{"derivedFrom":[makeQuery(id+"F15.boolean.opBoolean","MERGE",FACE,{"derivedFrom":[makeQuery(id+"F13.boolean.opBoolean","MERGE",FACE,{"derivedFrom":[makeQuery(id+"F11.boolean.opBoolean","MERGE",FACE,{"derivedFrom":[makeQuery(id+"F9.boolean.opBoolean","MERGE",FACE,{"derivedFrom":[makeQuery(id+"F7.boolean.opBoolean","MERGE",FACE,{"derivedFrom":[makeQuery(id+"F5.boolean.opBoolean","MERGE",FACE,{"derivedFrom":[makeQuery(id+"F3.boolean.opBoolean","MERGE",FACE,{"derivedFrom":[makeQuery(id+"F1.opExtrude","CAP_FACE",FACE,{"disambiguationData":[OSD([subQ13,subQ12,subQ11,subQ10])],"isStart":true}),makeQuery(id+"F3.opExtrude","CAP_FACE",FACE,{"disambiguationData":[OSD([subQ13,subQ12,subQ11,subQ10])],"isStart":false})]}),makeQuery(id+"F5.opExtrude","SWEPT_FACE",FACE,{"disambiguationData":[OSD([subQ9])]})]}),makeQuery(id+"F7.opExtrude","SWEPT_FACE",FACE,{"disambiguationData":[OSD([subQ8])]})]}),makeQuery(id+"F9.opExtrude","SWEPT_FACE",FACE,{"disambiguationData":[OSD([subQ7])]})]}),makeQuery(id+"F11.opExtrude","SWEPT_FACE",FACE,{"disambiguationData":[OSD([subQ6])]})]}),makeQuery(id+"F13.opExtrude","SWEPT_FACE",FACE,{"disambiguationData":[OSD([subQ5])]})]}),makeQuery(id+"F15.opExtrude","SWEPT_FACE",FACE,{"disambiguationData":[OSD([subQ4])]})]}),makeQuery(id+"F17.opExtrude","SWEPT_FACE",FACE,{"disambiguationData":[OSD([subQ3])]})]}),makeQuery(id+"F19.opExtrude","SWEPT_FACE",FACE,{"disambiguationData":[OSD([subQ2])]})]}),makeQuery(id+"F21.opExtrude","SWEPT_FACE",FACE,{"disambiguationData":[OSD([subQ1])]})]}),makeQuery(id+"F23.opExtrude","SWEPT_FACE",FACE,{"disambiguationData":[OSD([subQ0])]})]}),makeQuery(id+"F25.opExtrude","CAP_FACE",FACE,{"disambiguationData":[OSD([subQ13,subQ12,subQ11,subQ10,subQ9,subQ8,subQ7,subQ6,subQ5,subQ4,subQ3,subQ2,subQ1,subQ0])],"isStart":false})]}),makeQuery(id+"F29.opExtrude","SWEPT_FACE",FACE,{"disambiguationData":[OSD([sQuery(id+"F28.wireOp",EDGE,"E25.bottom")])]})]});}
            var sketch = newSketch(context, id + "F38", { "sketchPlane" : qUnion([Q0])});
            skLineSegment(sketch, "E30", {"start": v(-2639.65, -6477) * mm, "end": v(0, -4953) * mm});
            skLineSegment(sketch, "E31", {"start": v(0, -4953) * mm, "end": v(0, 6646.22) * mm});
            skLineSegment(sketch, "E32", {"start": v(0, 6646.22) * mm, "end": v(7031.5, 6646.22) * mm});
            skLineSegment(sketch, "E33", {"start": v(7031.5, 6646.22) * mm, "end": v(7031.5, 8531.05) * mm});
            skLineSegment(sketch, "E34", {"start": v(7031.5, 8531.05) * mm, "end": v(13933.88, 8470.59) * mm});
            skLineSegment(sketch, "E35", {"start": v(13933.88, 8470.59) * mm, "end": v(13881.69, 2511.67) * mm});
            skLineSegment(sketch, "E36", {"start": v(13881.69, 2511.67) * mm, "end": v(-2401.52, -6889.44) * mm});
            skLineSegment(sketch, "E37", {"start": v(-2401.52, -6889.44) * mm, "end": v(-2639.65, -6477) * mm});
            skSolve(sketch);
        }
        {
            var Q0;
            Q0 = qSketchRegion(id + "F38", true);
            extrude(context, id + "F39", {"entities" : qUnion([Q0]), "depth" : 25.4 * mm, "offsetDistance" : 25.4 * mm});
        }
    });
